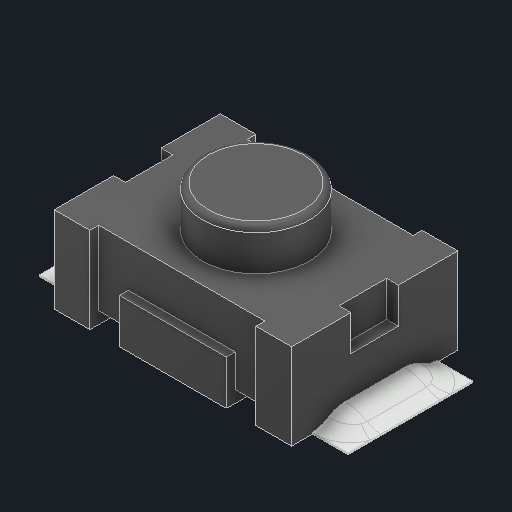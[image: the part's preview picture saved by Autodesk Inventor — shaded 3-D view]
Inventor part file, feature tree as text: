
AUTODESK INVENTOR PART (.ipt)
format: ipt  version: 2023 (Build 270158000, 158)  size: 214,016 bytes
history: native  units: in
note: dims shown in document units (in); Inventor stores cm internally (conversion verified against a paired STEP export)
features: fillet x1
ambient origin geometry x8: Origin, YZ Plane, XZ Plane, XY Plane, X Axis, Y Axis, Z Axis, Center Point
bodies: Solid1 (feature_tree)
feature tree (1):
  fillet  "Fillet3"  [1 undecoded]
note: 1 required parameter value undecoded (feature->parameter linkage not recoverable at this tier; creation-order binding heuristic only, values carry confidence <= 0.55)
